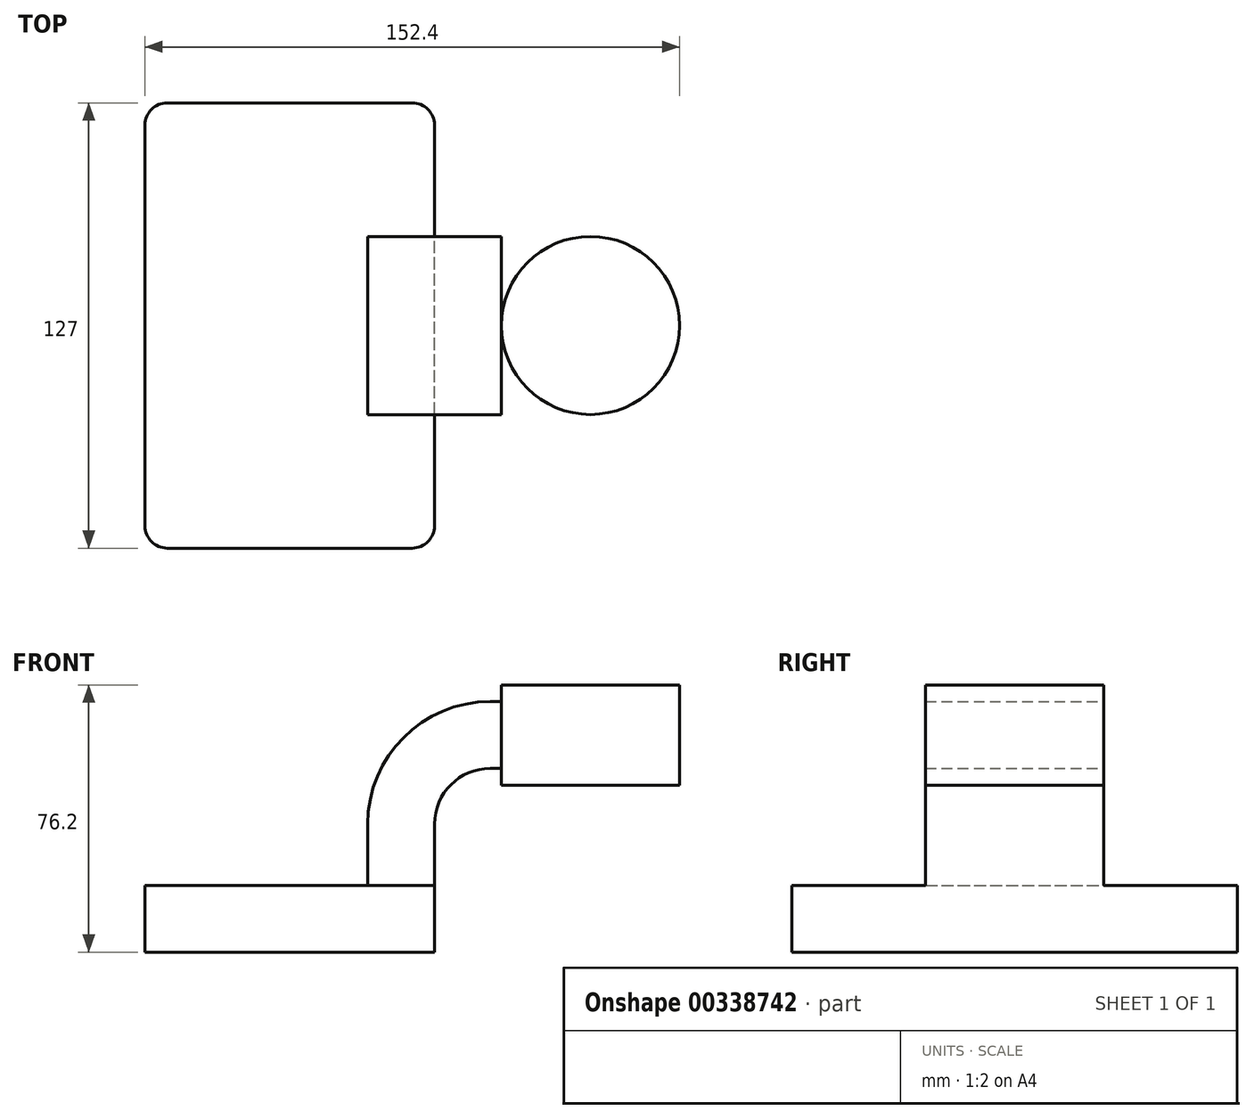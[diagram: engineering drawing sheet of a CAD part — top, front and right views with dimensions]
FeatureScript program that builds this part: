
annotation { "Feature Type Name" : "Feature", "Feature Type Description" : "" }
export const myFeature = defineFeature(function(context is Context, id is Id, definition is map)
    precondition{}
    {
        {
            var Q0;
            Q0=qCreatedBy(makeId("Front.planeOp"),FACE);
            var sketch = newSketch(context, id + "F0", { "sketchPlane" : qUnion([Q0])});
            skLineSegment(sketch, "E0.bottom", {"start": v(0, 0) * mm, "end": v(82.55, 0) * mm});
            skLineSegment(sketch, "E0.top", {"start": v(0, 19.05) * mm, "end": v(82.55, 19.05) * mm});
            skLineSegment(sketch, "E0.left", {"start": v(0, 0) * mm, "end": v(0, 19.05) * mm});
            skLineSegment(sketch, "E0.right", {"start": v(82.55, 0) * mm, "end": v(82.55, 19.05) * mm});
            skLineSegment(sketch, "E1", {"start": v(82.55, 19.05) * mm, "end": v(82.55, 36.53) * mm});
            skArc(sketch, "E2", {"start": v(82.55, 36.53) * mm, "mid": v(87.2, 47.75) * mm, "end": v(98.43, 52.4) * mm});
            skLineSegment(sketch, "E3", {"start": v(98.43, 52.4) * mm, "end": v(126.66, 52.4) * mm});
            skLineSegment(sketch, "E4.bottom", {"start": v(152.4, 76.2) * mm, "end": v(101.6, 76.2) * mm});
            skLineSegment(sketch, "E4.top", {"start": v(152.4, 47.62) * mm, "end": v(101.6, 47.62) * mm});
            skLineSegment(sketch, "E4.left", {"start": v(152.4, 76.2) * mm, "end": v(152.4, 47.62) * mm});
            skLineSegment(sketch, "E4.right", {"start": v(101.6, 76.2) * mm, "end": v(101.6, 47.62) * mm});
            skPoint(sketch, "E4.middle", {"position": v(127, 61.91) * mm});
            skLineSegment(sketch, "E5.0", {"start": v(98.43, 71.45) * mm, "end": v(127, 71.45) * mm});
            skArc(sketch, "E5.1", {"start": v(63.5, 36.53) * mm, "mid": v(73.73, 61.22) * mm, "end": v(98.43, 71.45) * mm});
            skLineSegment(sketch, "E5.2", {"start": v(63.5, 19.05) * mm, "end": v(63.5, 36.53) * mm});
            skLineSegment(sketch, "E6", {"start": v(127, 47.62) * mm, "end": v(127, 76.2) * mm});
            skFitSpline(sketch, "E7", {"points": [v(0, 19.05) * mm, v(98.43, 71.45) * mm], "startDerivative": vector(34.35, 105.82) * mm, "endDerivative": vector(162.55, -19.61) * mm});
            skSolve(sketch);
        }
        {
            var Q0;
            Q0=makeQuery(id+"F0.imprint","IMPRINT",FACE,{"disambiguationData":[TD([[makeQuery(id+"F0.imprint","IMPRINT",EDGE,{"derivedFrom":sQuery(id+"F0.wireOp",EDGE,"E0.bottom")}),1.0]])]});
            extrude(context, id + "F1", {"entities" : qUnion([Q0]), "endBound" : BoundingType.SYMMETRIC, "depth" : 127 * mm});
        }
        {
            var Q0;
            {var subQ2=sQuery(id+"F0.wireOp",EDGE,"E1");Q0=makeQuery(id+"F0.imprint","IMPRINT",FACE,{"disambiguationData":[TD([[makeQuery(id+"F0.imprint","IMPRINT",EDGE,{"derivedFrom":subQ2}),1.0]])]});}
            extrude(context, id + "F2", {"entities" : qUnion([Q0]), "operationType" : NewBodyOperationType.ADD, "endBound" : BoundingType.SYMMETRIC, "depth" : 50.8 * mm});
        }
        {
            var Q0;
            Q0=makeQuery(id+"F0.imprint","IMPRINT",FACE,{"disambiguationData":[TD([[makeQuery(id+"F0.imprint","IMPRINT",EDGE,{"derivedFrom":sQuery(id+"F0.wireOp",EDGE,"E5.1")}),1.0]])]});
            extrude(context, id + "F3", {"entities" : qUnion([Q0]), "operationType" : NewBodyOperationType.ADD, "endBound" : BoundingType.SYMMETRIC, "depth" : 15.88 * mm});
        }
        {
            var Q0;
            {var subQ0=sQuery(id+"F0.wireOp",EDGE,"E4.left");Q0=makeQuery(id+"F0.imprint","IMPRINT",FACE,{"disambiguationData":[TD([[makeQuery(id+"F0.imprint","IMPRINT",EDGE,{"derivedFrom":subQ0}),-1.0]])]});}
            var Q1;
            Q1=sQuery(id+"F0.wireOp",EDGE,"E6");
            revolve(context, id + "F4", {"operationType" : NewBodyOperationType.ADD, "entities" : qUnion([Q0]), "axis" : qUnion([Q1]), "revolveType" : RevolveType.FULL});
        }
        {
            var Q0;
            Q0=makeQuery(id+"F1.opExtrude","CAP_EDGE",EDGE,{"disambiguationData":[OSD([sQuery(id+"F0.wireOp",EDGE,"E0.right")])],"isStart":false});
            var Q1;
            Q1=makeQuery(id+"F1.opExtrude","CAP_EDGE",EDGE,{"disambiguationData":[OSD([sQuery(id+"F0.wireOp",EDGE,"E0.left")])],"isStart":true});
            var Q2;
            Q2=makeQuery(id+"F1.opExtrude","CAP_EDGE",EDGE,{"disambiguationData":[OSD([sQuery(id+"F0.wireOp",EDGE,"E0.right")])],"isStart":true});
            var Q3;
            Q3=makeQuery(id+"F1.opExtrude","CAP_EDGE",EDGE,{"disambiguationData":[OSD([sQuery(id+"F0.wireOp",EDGE,"E0.left")])],"isStart":false});
            fillet(context, id + "F5", {"entities" : qUnion([Q0, Q1, Q2, Q3]), "radius" : 6.35 * mm, "tangentPropagation" : true, "allowEdgeOverflow" : false});
        }
    });
